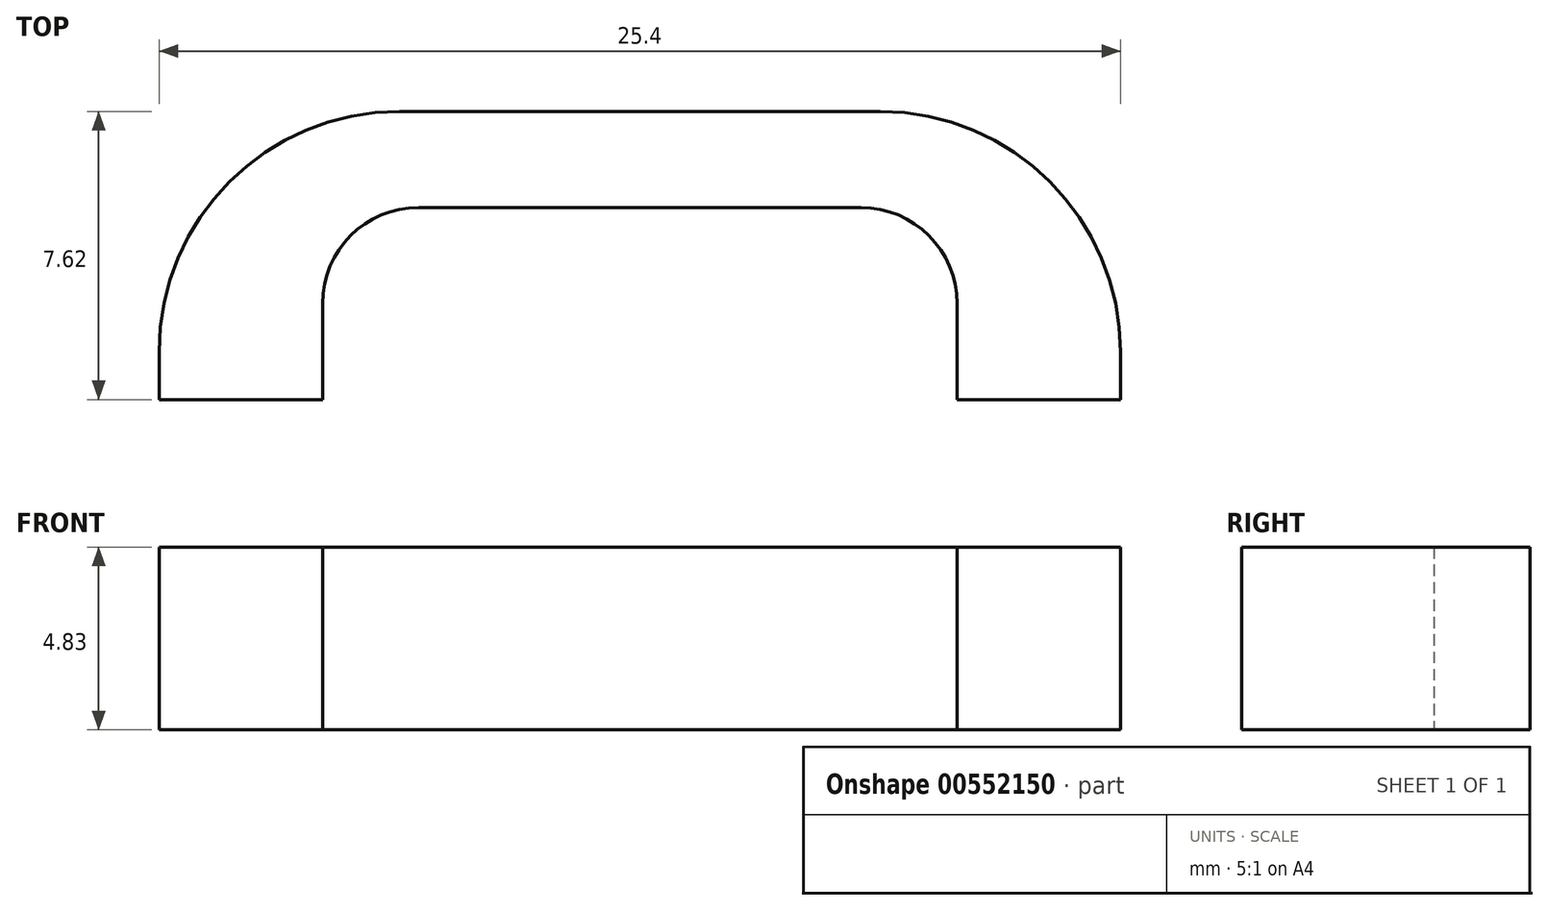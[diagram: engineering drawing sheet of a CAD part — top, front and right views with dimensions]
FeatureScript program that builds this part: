
annotation { "Feature Type Name" : "Feature", "Feature Type Description" : "" }
export const myFeature = defineFeature(function(context is Context, id is Id, definition is map)
    precondition{}
    {
        {
            var Q0;
            Q0=qCreatedBy(makeId("Top.planeOp"),FACE);
            var sketch = newSketch(context, id + "F0", { "sketchPlane" : qUnion([Q0])});
            skLineSegment(sketch, "E0", {"start": v(-11.8, 5.08) * mm, "end": v(-11.8, 6.35) * mm});
            skLineSegment(sketch, "E1", {"start": v(-5.45, 12.7) * mm, "end": v(7.25, 12.7) * mm});
            skLineSegment(sketch, "E2", {"start": v(13.6, 6.35) * mm, "end": v(13.6, 5.08) * mm});
            skLineSegment(sketch, "E3", {"start": v(-11.8, 5.08) * mm, "end": v(-7.49, 5.08) * mm});
            skLineSegment(sketch, "E4", {"start": v(-7.49, 5.08) * mm, "end": v(-7.49, 7.62) * mm});
            skLineSegment(sketch, "E5", {"start": v(-4.95, 10.16) * mm, "end": v(6.74, 10.16) * mm});
            skLineSegment(sketch, "E6", {"start": v(9.28, 7.62) * mm, "end": v(9.28, 5.08) * mm});
            skLineSegment(sketch, "E7", {"start": v(9.28, 5.08) * mm, "end": v(13.6, 5.08) * mm});
            skPoint(sketch, "E8.visualSharp", {"position": v(-7.49, 10.16) * mm});
            skArc(sketch, "E8.filletArc", {"start": v(-4.95, 10.16) * mm, "mid": v(-6.74, 9.42) * mm, "end": v(-7.49, 7.62) * mm});
            skPoint(sketch, "E9.visualSharp", {"position": v(9.28, 10.16) * mm});
            skArc(sketch, "E9.filletArc", {"start": v(9.28, 7.62) * mm, "mid": v(8.53, 9.42) * mm, "end": v(6.74, 10.16) * mm});
            skPoint(sketch, "E10.visualSharp", {"position": v(-11.8, 12.7) * mm});
            skArc(sketch, "E10.filletArc", {"start": v(-5.45, 12.7) * mm, "mid": v(-9.94, 10.84) * mm, "end": v(-11.8, 6.35) * mm});
            skPoint(sketch, "E11.visualSharp", {"position": v(13.6, 12.7) * mm});
            skArc(sketch, "E11.filletArc", {"start": v(13.6, 6.35) * mm, "mid": v(11.74, 10.84) * mm, "end": v(7.25, 12.7) * mm});
            skSolve(sketch);
        }
        {
            var Q0;
            Q0=makeQuery(id+"F0.imprint","IMPRINT",FACE,{"disambiguationData":[TD([[makeQuery(id+"F0.imprint","IMPRINT",EDGE,{"derivedFrom":sQuery(id+"F0.wireOp",EDGE,"E0")}),-1.0]])]});
            extrude(context, id + "F1", {"entities" : qUnion([Q0]), "depth" : 4.83 * mm, "offsetDistance" : 25.4 * mm});
        }
    });
